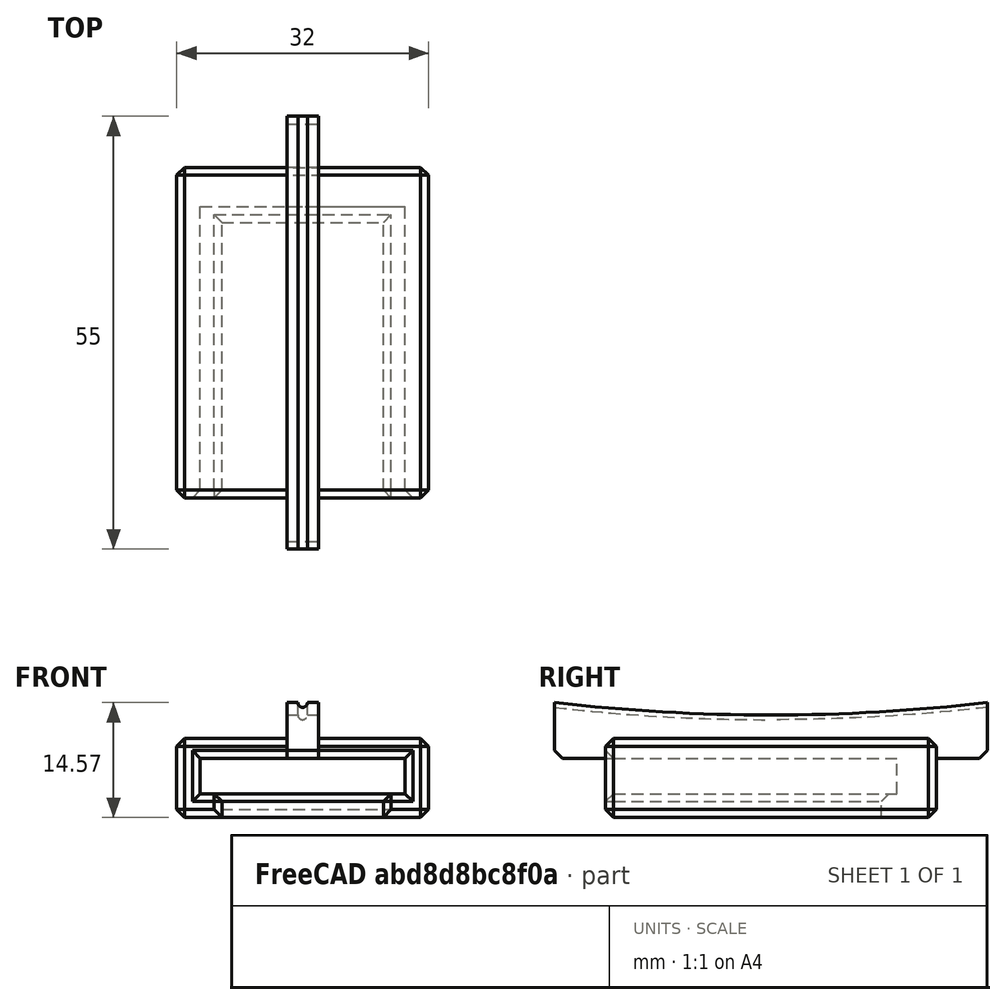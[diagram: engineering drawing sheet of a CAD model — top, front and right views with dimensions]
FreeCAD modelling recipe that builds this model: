
FCSTD DOCUMENT  (FreeCAD 0.21R33694 (Git))
Label: fret_wire_clamp_top
License: All rights reserved
LicenseURL: http://en.wikipedia.org/wiki/All_rights_reserved
objects: Part::Box×4, Part::MultiFuse×3, Part::Cut×2, Part::Chamfer×2, Spreadsheet::Sheet×1, Part::Torus×1, Part::Cylinder×1
note: 13 computed .brp shape members not serialized (recipe doc carries the construction recipe); baked Part::Feature solids carry a one-line shape summary decoded from their .brp

FEATURE [Spreadsheet::Sheet] Spreadsheet
  cells = A1='neck_width; B1(neck_width)=55; A2='neck_support_transform; B2(neck_support_transform)==21 - neck_width / 2; A4='disc_center_h; B4(disc_center_h)=21; A5='disc_center_v; B5(disc_center_v)==disc_radius + 13; A6='disc_radius; B6(disc_radius)=241; A8='disc_fill_radius; B8(disc_fill_radius)==disc_radius
FEATURE [Part::Box] Box  label="mount_body"
  AttacherType = Attacher::AttachEngine3D
  Height = 10
  Length = 32
  Placement = pos=(-1,0,0) rot=(0,0,1;0rad)
  Width = 42
FEATURE [Part::Box] Box001  label="clamp_mount_hole"
  AttacherType = Attacher::AttachEngine3D
  Height = 3
  Length = 20.5
  Placement = pos=(4.75,0,0) rot=(0,0,1;0rad)
  Width = 35
FEATURE [Part::Box] Box002  label="clamp_mount_rail"
  AttacherType = Attacher::AttachEngine3D
  Height = 4.5
  Length = 26
  Placement = pos=(2,0,3) rot=(0,0,1;0rad)
  Width = 37
FEATURE [Part::MultiFuse] Fusion  label="clamp_mount_shape"
  Shapes = -> [Box002,Box001]
FEATURE [Part::Cut] Cut  label="clamp_mount_body"
  Base = -> Box
  Tool = -> Fusion
FEATURE [Part::Box] Box003  label="neck_support"
  AttacherType = Attacher::AttachEngine3D
  Height = 20
  Length = 4
  Placement = pos=(13,-6.5,7.5) rot=(0,0,1;0rad)
  Width = 55
  expr: .Placement.Base.y = Spreadsheet.neck_support_transform
  expr: Width = Spreadsheet.neck_width
FEATURE [Part::Torus] Torus
  Angle1 = -180
  Angle2 = 180
  Angle3 = 360
  AttacherType = Attacher::AttachEngine3D
  Placement = pos=(15,0,0) rot=(0,1,0;1.5708rad)
  Radius1 = 241
  Radius2 = 0.6
  expr: Radius1 = Spreadsheet.disc_radius
FEATURE [Part::Cylinder] Cylinder
  Angle = 360
  AttacherType = Attacher::AttachEngine3D
  FirstAngle = 0
  Height = 10
  Placement = pos=(10,0,0) rot=(0,1,0;1.5708rad)
  Radius = 241
  SecondAngle = 0
  expr: Radius = Spreadsheet.disc_fill_radius
FEATURE [Part::MultiFuse] Fusion001  label="cut_disk"
  Placement = pos=(0,21,254) rot=(0,0,1;0rad)
  Shapes = -> [Torus,Cylinder]
  expr: .Placement.Base.y = Spreadsheet.disc_center_h
  expr: .Placement.Base.z = Spreadsheet.disc_center_v
FEATURE [Part::Cut] Cut001  label="fret_press_body"
  Base = -> Box003
  Tool = -> Fusion001
FEATURE [Part::Chamfer] Chamfer  label="fret_press_body_camfer"
  Base = -> Cut001
  Edges = 2 edges r=1: [Edge11,Edge20]
FEATURE [Part::Chamfer] Chamfer001  label="clamp_mount_body_camfer"
  Base = -> Cut
  Edges = 23 edges r=1: [Edge1,Edge2,Edge3,Edge4,Edge5,Edge6,Edge7,Edge8,Edge9,Edge10,Edge11,Edge12,Edge13,Edge14,Edge15,Edge16,Edge17,Edge18,Edge19,Edge20,Edge24,Edge28,Edge29]
FEATURE [Part::MultiFuse] Fusion002  label="fret_wire_clamp"
  Shapes = -> [Chamfer,Chamfer001]
